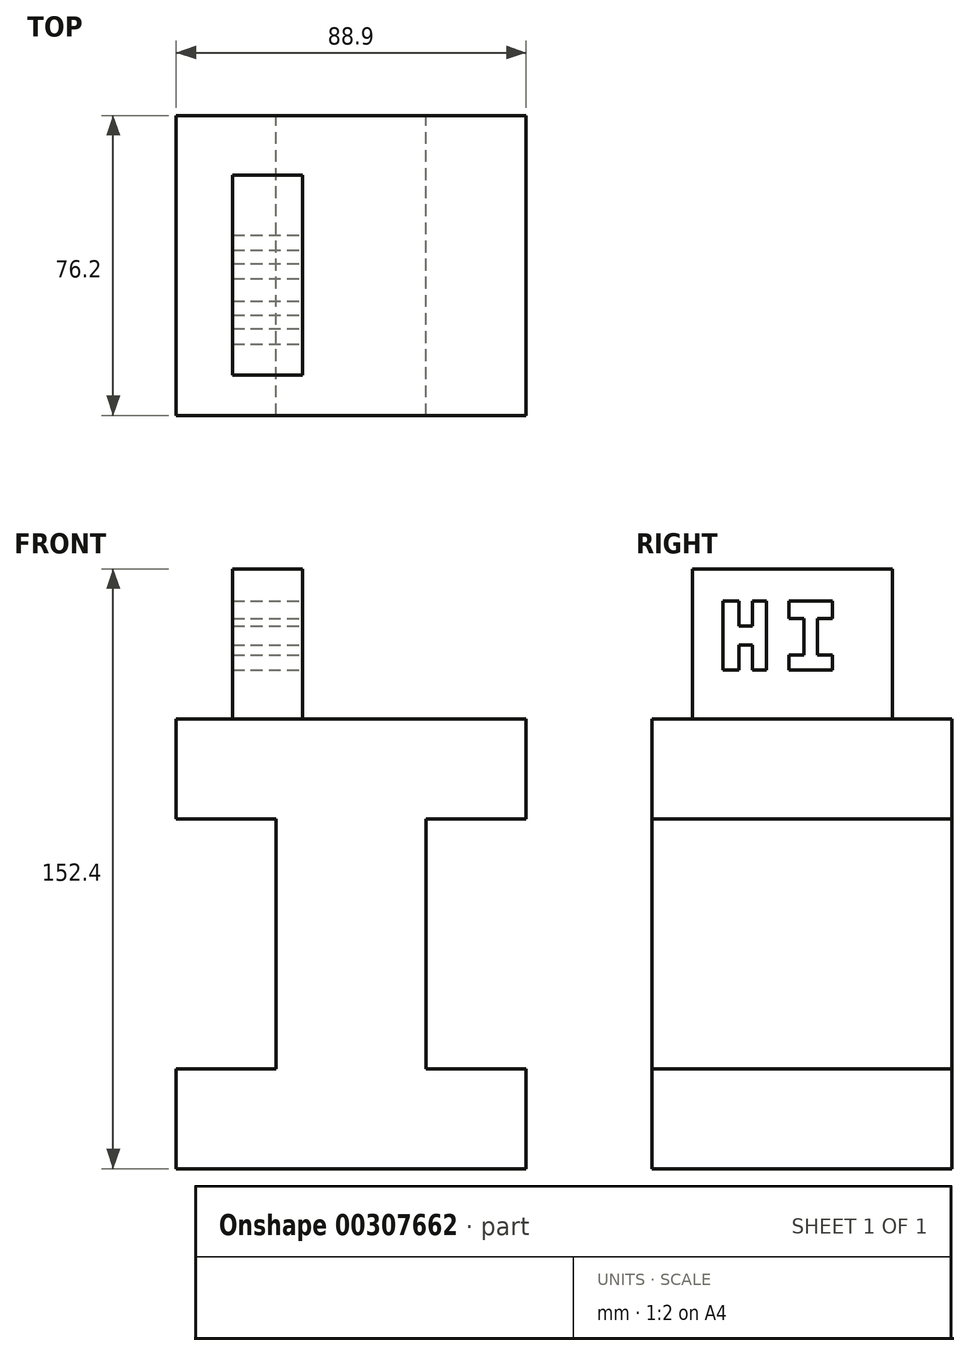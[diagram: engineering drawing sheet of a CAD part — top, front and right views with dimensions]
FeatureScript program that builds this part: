
annotation { "Feature Type Name" : "Feature", "Feature Type Description" : "" }
export const myFeature = defineFeature(function(context is Context, id is Id, definition is map)
    precondition{}
    {
        {
            var Q0;
            Q0=qCreatedBy(makeId("Front.planeOp"),FACE);
            var sketch = newSketch(context, id + "F0", { "sketchPlane" : qUnion([Q0])});
            skLineSegment(sketch, "E0", {"start": v(-44.75, -44.58) * mm, "end": v(44.15, -44.58) * mm});
            skLineSegment(sketch, "E1", {"start": v(44.15, -44.58) * mm, "end": v(44.15, -19.18) * mm});
            skLineSegment(sketch, "E2", {"start": v(44.15, -19.18) * mm, "end": v(18.75, -19.18) * mm});
            skLineSegment(sketch, "E3", {"start": v(18.75, -19.18) * mm, "end": v(18.75, 44.32) * mm});
            skLineSegment(sketch, "E4", {"start": v(18.75, 44.32) * mm, "end": v(44.15, 44.32) * mm});
            skLineSegment(sketch, "E5", {"start": v(44.15, 44.32) * mm, "end": v(44.15, 69.72) * mm});
            skLineSegment(sketch, "E6", {"start": v(44.15, 69.72) * mm, "end": v(-44.75, 69.72) * mm});
            skLineSegment(sketch, "E7", {"start": v(-44.75, 69.72) * mm, "end": v(-44.75, 44.32) * mm});
            skLineSegment(sketch, "E8", {"start": v(-44.75, 44.32) * mm, "end": v(-19.35, 44.32) * mm});
            skLineSegment(sketch, "E9", {"start": v(-19.35, 44.32) * mm, "end": v(-19.35, -19.18) * mm});
            skLineSegment(sketch, "E10", {"start": v(-19.35, -19.18) * mm, "end": v(-44.75, -19.18) * mm});
            skLineSegment(sketch, "E11", {"start": v(-44.75, -19.18) * mm, "end": v(-44.75, -44.58) * mm});
            skSolve(sketch);
        }
        {
            var Q0;
            Q0=makeQuery(id+"F0.imprint","IMPRINT",FACE,{"disambiguationData":[TD([[makeQuery(id+"F0.imprint","IMPRINT",EDGE,{"derivedFrom":sQuery(id+"F0.wireOp",EDGE,"E0")}),1.0]])]});
            extrude(context, id + "F1", {"entities" : qUnion([Q0]), "depth" : 76.2 * mm});
        }
        {
            var Q0;
            Q0=makeQuery(id+"F1.opExtrude","SWEPT_FACE",FACE,{"disambiguationData":[OSD([sQuery(id+"F0.wireOp",EDGE,"E6")])]});
            var sketch = newSketch(context, id + "F2", { "sketchPlane" : qUnion([Q0])});
            skLineSegment(sketch, "E12", {"start": v(-30.4, -15.11) * mm, "end": v(-30.4, -65.91) * mm});
            skLineSegment(sketch, "E13", {"start": v(-30.4, -65.91) * mm, "end": v(-12.62, -65.91) * mm});
            skLineSegment(sketch, "E14", {"start": v(-12.62, -65.91) * mm, "end": v(-12.62, -15.11) * mm});
            skLineSegment(sketch, "E15", {"start": v(-12.62, -15.11) * mm, "end": v(-30.4, -15.11) * mm});
            skSolve(sketch);
        }
        {
            var Q0;
            Q0=makeQuery(id+"F2.imprint","IMPRINT",FACE,{"disambiguationData":[TD([[makeQuery(id+"F2.imprint","IMPRINT",EDGE,{"derivedFrom":sQuery(id+"F2.wireOp",EDGE,"E12")}),1.0]])]});
            extrude(context, id + "F3", {"entities" : qUnion([Q0]), "operationType" : NewBodyOperationType.ADD, "depth" : 38.1 * mm});
        }
        {
            var Q0;
            Q0=makeQuery(id+"F3.opExtrude","SWEPT_FACE",FACE,{"disambiguationData":[OSD([sQuery(id+"F2.wireOp",EDGE,"E14")])]});
            var sketch = newSketch(context, id + "F4", { "sketchPlane" : qUnion([Q0])});
            skLineSegment(sketch, "E16", {"start": v(-58.16, 99.7) * mm, "end": v(-58.16, 82.12) * mm});
            skLineSegment(sketch, "E17", {"start": v(-58.16, 82.12) * mm, "end": v(-54.2, 82.12) * mm});
            skLineSegment(sketch, "E18", {"start": v(-54.2, 82.12) * mm, "end": v(-54.2, 88.47) * mm});
            skLineSegment(sketch, "E19", {"start": v(-54.2, 88.47) * mm, "end": v(-50.7, 88.47) * mm});
            skLineSegment(sketch, "E20", {"start": v(-50.7, 88.47) * mm, "end": v(-50.7, 82.12) * mm});
            skLineSegment(sketch, "E21", {"start": v(-50.7, 82.12) * mm, "end": v(-47.12, 82.12) * mm});
            skLineSegment(sketch, "E22", {"start": v(-47.12, 82.12) * mm, "end": v(-47.12, 99.7) * mm});
            skLineSegment(sketch, "E23", {"start": v(-47.12, 99.7) * mm, "end": v(-50.7, 99.7) * mm});
            skLineSegment(sketch, "E24", {"start": v(-50.7, 99.7) * mm, "end": v(-50.7, 93.34) * mm});
            skLineSegment(sketch, "E25", {"start": v(-50.7, 93.34) * mm, "end": v(-54.2, 93.34) * mm});
            skLineSegment(sketch, "E26", {"start": v(-54.2, 93.34) * mm, "end": v(-54.2, 99.7) * mm});
            skLineSegment(sketch, "E27", {"start": v(-54.2, 99.7) * mm, "end": v(-58.16, 99.7) * mm});
            skSolve(sketch);
        }
        {
            var Q0;
            Q0=makeQuery(id+"F4.imprint","IMPRINT",FACE,{"disambiguationData":[TD([[makeQuery(id+"F4.imprint","IMPRINT",EDGE,{"derivedFrom":sQuery(id+"F4.wireOp",EDGE,"E16")}),1.0]])]});
            extrude(context, id + "F5", {"entities" : qUnion([Q0]), "operationType" : NewBodyOperationType.REMOVE, "oppositeDirection" : true, "depth" : 63.5 * mm});
        }
        {
            var Q0;
            Q0=makeQuery(id+"F3.opExtrude","SWEPT_FACE",FACE,{"disambiguationData":[OSD([sQuery(id+"F2.wireOp",EDGE,"E14")])]});
            var sketch = newSketch(context, id + "F6", { "sketchPlane" : qUnion([Q0])});
            skLineSegment(sketch, "E28", {"start": v(-30.37, 95.23) * mm, "end": v(-34.18, 95.23) * mm});
            skLineSegment(sketch, "E29", {"start": v(-34.18, 95.23) * mm, "end": v(-34.18, 85.97) * mm});
            skLineSegment(sketch, "E30", {"start": v(-34.18, 85.97) * mm, "end": v(-30.37, 85.97) * mm});
            skLineSegment(sketch, "E31", {"start": v(-30.37, 85.97) * mm, "end": v(-30.37, 82.12) * mm});
            skLineSegment(sketch, "E32", {"start": v(-30.37, 82.12) * mm, "end": v(-41.47, 82.12) * mm});
            skLineSegment(sketch, "E33", {"start": v(-41.47, 82.12) * mm, "end": v(-41.47, 85.97) * mm});
            skLineSegment(sketch, "E34", {"start": v(-41.47, 85.97) * mm, "end": v(-37.66, 85.97) * mm});
            skLineSegment(sketch, "E35", {"start": v(-37.66, 85.97) * mm, "end": v(-37.66, 95.23) * mm});
            skLineSegment(sketch, "E36", {"start": v(-37.66, 95.23) * mm, "end": v(-41.47, 95.23) * mm});
            skLineSegment(sketch, "E37", {"start": v(-41.47, 95.23) * mm, "end": v(-41.47, 99.7) * mm});
            skPoint(sketch, "E37.endSnap0", {"position": v(-48.9, 99.7) * mm});
            skLineSegment(sketch, "E38", {"start": v(-41.47, 99.7) * mm, "end": v(-30.37, 99.7) * mm});
            skLineSegment(sketch, "E39", {"start": v(-30.37, 99.7) * mm, "end": v(-30.37, 95.23) * mm});
            skSolve(sketch);
        }
        {
            var Q0;
            Q0=makeQuery(id+"F6.imprint","IMPRINT",FACE,{"disambiguationData":[TD([[makeQuery(id+"F6.imprint","IMPRINT",EDGE,{"derivedFrom":sQuery(id+"F6.wireOp",EDGE,"E28")}),-1.0]])]});
            extrude(context, id + "F7", {"entities" : qUnion([Q0]), "operationType" : NewBodyOperationType.REMOVE, "oppositeDirection" : true, "depth" : 63.5 * mm});
        }
    });
